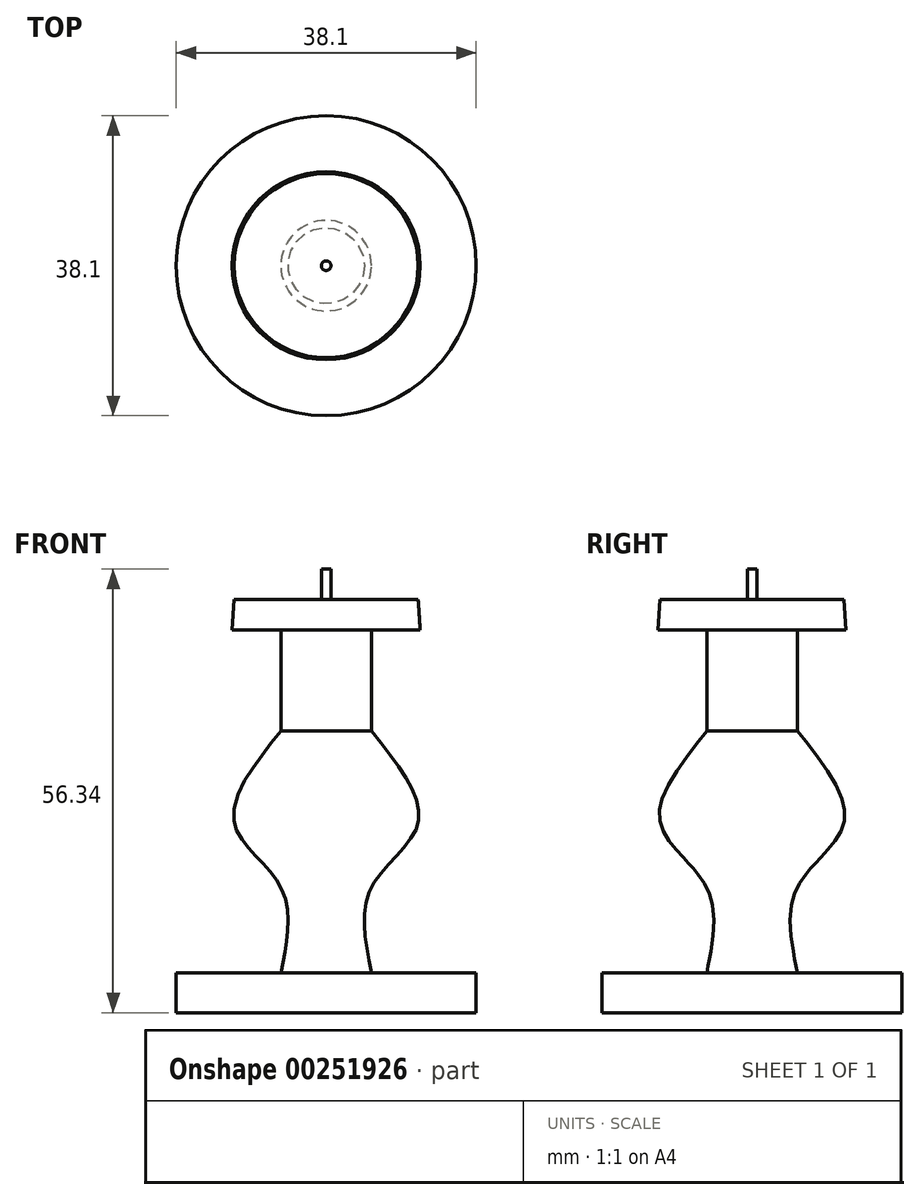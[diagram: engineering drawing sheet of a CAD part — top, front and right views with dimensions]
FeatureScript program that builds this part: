
annotation { "Feature Type Name" : "Feature", "Feature Type Description" : "" }
export const myFeature = defineFeature(function(context is Context, id is Id, definition is map)
    precondition{}
    {
        {
            var Q0;
            Q0=qCreatedBy(makeId("Front.planeOp"),FACE);
            var sketch = newSketch(context, id + "F0", { "sketchPlane" : qUnion([Q0])});
            skLineSegment(sketch, "E0", {"start": v(0, 80.72) * mm, "end": v(0, -82.1) * mm, "construction": true});
            skLineSegment(sketch, "E1", {"start": v(-19.05, -74.72) * mm, "end": v(-19.05, -69.64) * mm});
            skLineSegment(sketch, "E2", {"start": v(-19.05, -69.64) * mm, "end": v(0, -69.64) * mm});
            skLineSegment(sketch, "E3", {"start": v(-19.05, -74.72) * mm, "end": v(0, -74.72) * mm});
            skLineSegment(sketch, "E4", {"start": v(-5.76, -74.72) * mm, "end": v(-5.76, -69.64) * mm});
            skFitSpline(sketch, "E5", {"points": [v(-5.76, -69.64) * mm, v(-5.76, -58.8) * mm, v(-11.69, -50.56) * mm, v(-5.76, -38.96) * mm], "startDerivative": vector(7.3, 35.53) * mm, "endDerivative": vector(27.82, 34.69) * mm});
            skLineSegment(sketch, "E6", {"start": v(-5.76, -38.96) * mm, "end": v(-5.76, -26.08) * mm});
            skLineSegment(sketch, "E7", {"start": v(-5.76, -26.08) * mm, "end": v(-11.94, -26.08) * mm});
            skLineSegment(sketch, "E8", {"start": v(-11.94, -26.08) * mm, "end": v(-11.69, -22.21) * mm});
            skLineSegment(sketch, "E9", {"start": v(-11.69, -22.21) * mm, "end": v(0, -22.21) * mm});
            skLineSegment(sketch, "E10", {"start": v(0, -22.21) * mm, "end": v(0, -74.72) * mm});
            skLineSegment(sketch, "E11", {"start": v(-0.6, -22.21) * mm, "end": v(-0.6, -18.38) * mm});
            skLineSegment(sketch, "E12", {"start": v(-0.6, -18.38) * mm, "end": v(0, -18.38) * mm});
            skLineSegment(sketch, "E13", {"start": v(0, -18.38) * mm, "end": v(0, -22.21) * mm});
            skLineSegment(sketch, "E14", {"start": v(0, -69.64) * mm, "end": v(0, -74.72) * mm});
            skLineSegment(sketch, "E15", {"start": v(-4.78, -74.72) * mm, "end": v(-5.76, -74.72) * mm});
            skSolve(sketch);
        }
        {
            var Q0;
            Q0 = qSketchRegion(id + "F0", true);
            var Q1;
            Q1=sQuery(id+"F0.wireOp",EDGE,"E0");
            revolve(context, id + "F1", {"entities" : qUnion([Q0]), "axis" : qUnion([Q1]), "revolveType" : RevolveType.FULL});
        }
    });
